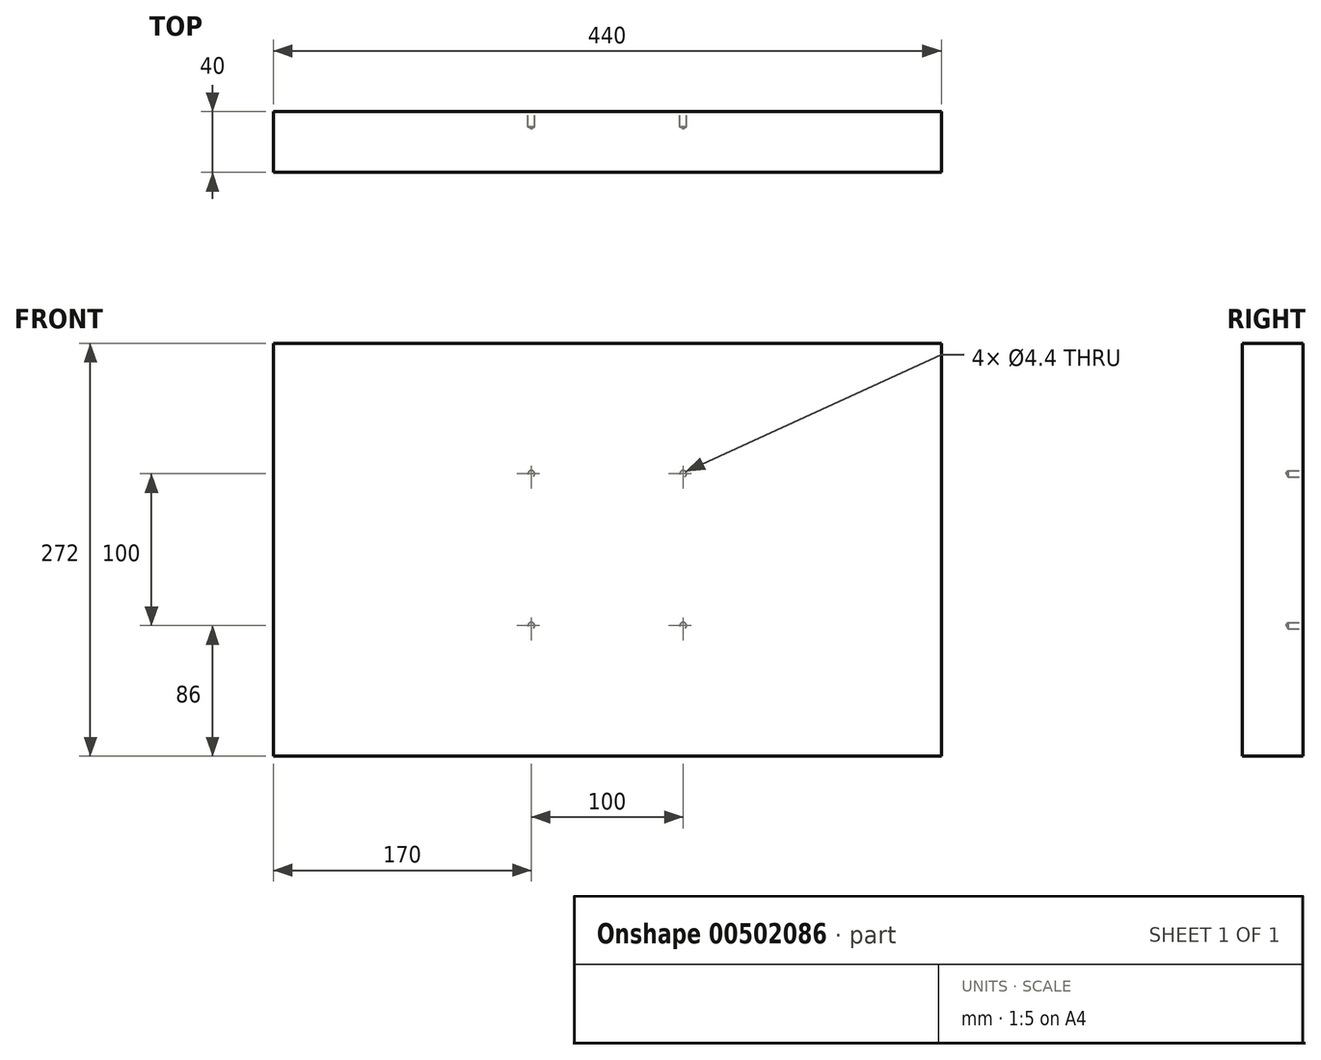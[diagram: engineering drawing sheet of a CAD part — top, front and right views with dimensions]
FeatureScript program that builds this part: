
annotation { "Feature Type Name" : "Feature", "Feature Type Description" : "" }
export const myFeature = defineFeature(function(context is Context, id is Id, definition is map)
    precondition{}
    {
        {
            var Q0;
            Q0=qCreatedBy(makeId("Front.planeOp"),FACE);
            var sketch = newSketch(context, id + "F0", { "sketchPlane" : qUnion([Q0])});
            skLineSegment(sketch, "E0.bottom", {"start": v(50, -50) * mm, "end": v(-50, -50) * mm, "construction": true});
            skLineSegment(sketch, "E0.top", {"start": v(50, 50) * mm, "end": v(-50, 50) * mm, "construction": true});
            skLineSegment(sketch, "E0.left", {"start": v(50, -50) * mm, "end": v(50, 50) * mm, "construction": true});
            skLineSegment(sketch, "E0.right", {"start": v(-50, -50) * mm, "end": v(-50, 50) * mm, "construction": true});
            skPoint(sketch, "E0.middle", {"position": v(0, 0) * mm});
            skLineSegment(sketch, "E1.bottom", {"start": v(-220, 136) * mm, "end": v(220, 136) * mm});
            skLineSegment(sketch, "E1.top", {"start": v(-220, -136) * mm, "end": v(220, -136) * mm});
            skLineSegment(sketch, "E1.left", {"start": v(-220, 136) * mm, "end": v(-220, -136) * mm});
            skLineSegment(sketch, "E1.right", {"start": v(220, 136) * mm, "end": v(220, -136) * mm});
            skSolve(sketch);
        }
        {
            var Q0;
            Q0=makeQuery(id+"F0.imprint","IMPRINT",FACE,{"disambiguationData":[TD([[makeQuery(id+"F0.imprint","IMPRINT",EDGE,{"derivedFrom":sQuery(id+"F0.wireOp",EDGE,"E1.bottom")}),-1.0]])]});
            extrude(context, id + "F1", {"entities" : qUnion([Q0]), "depth" : 40 * mm});
        }
        {
            var Q0;
            Q0=sQuery(id+"F0.wireOp",VERTEX,"E0.left.end");
            var Q1;
            Q1=sQuery(id+"F0.wireOp",VERTEX,"E0.right.end");
            var Q2;
            Q2=sQuery(id+"F0.wireOp",VERTEX,"E0.right.start");
            var Q3;
            Q3=sQuery(id+"F0.wireOp",VERTEX,"E0.bottom.start");
            var Q4;
            Q4=makeQuery(id+"F1.opExtrude","SWEPT_BODY",BODY,{"disambiguationData":[OSD([sQuery(id+"F0.wireOp",EDGE,"E1.bottom"),sQuery(id+"F0.wireOp",EDGE,"E1.top"),sQuery(id+"F0.wireOp",EDGE,"E1.left"),sQuery(id+"F0.wireOp",EDGE,"E1.right")])]});
            hole(context, id + "F2", {"style" : HoleStyle.SIMPLE, "endStyle" : HoleEndStyle.BLIND, "oppositeDirection" : true, "standardTappedOrClearance" : lookupTablePath({ "standard" : "ISO", "fit" : "Normal", "size" : "M4", "type" : "Clearance" }), "standardBlindInLast" : lookupTablePath({ "fit" : "Standard", "standard" : "ISO", "size" : "M4", "type" : "Clearance" }), "holeDiameter" : 4.4 * mm, "holeDepth" : 10 * mm, "isTappedThrough" : true, "tappedDepth" : 3 * mm, "tapClearance" : 3, "locations" : qUnion([Q0, Q1, Q2, Q3]), "scope" : qUnion([Q4])});
        }
    });
